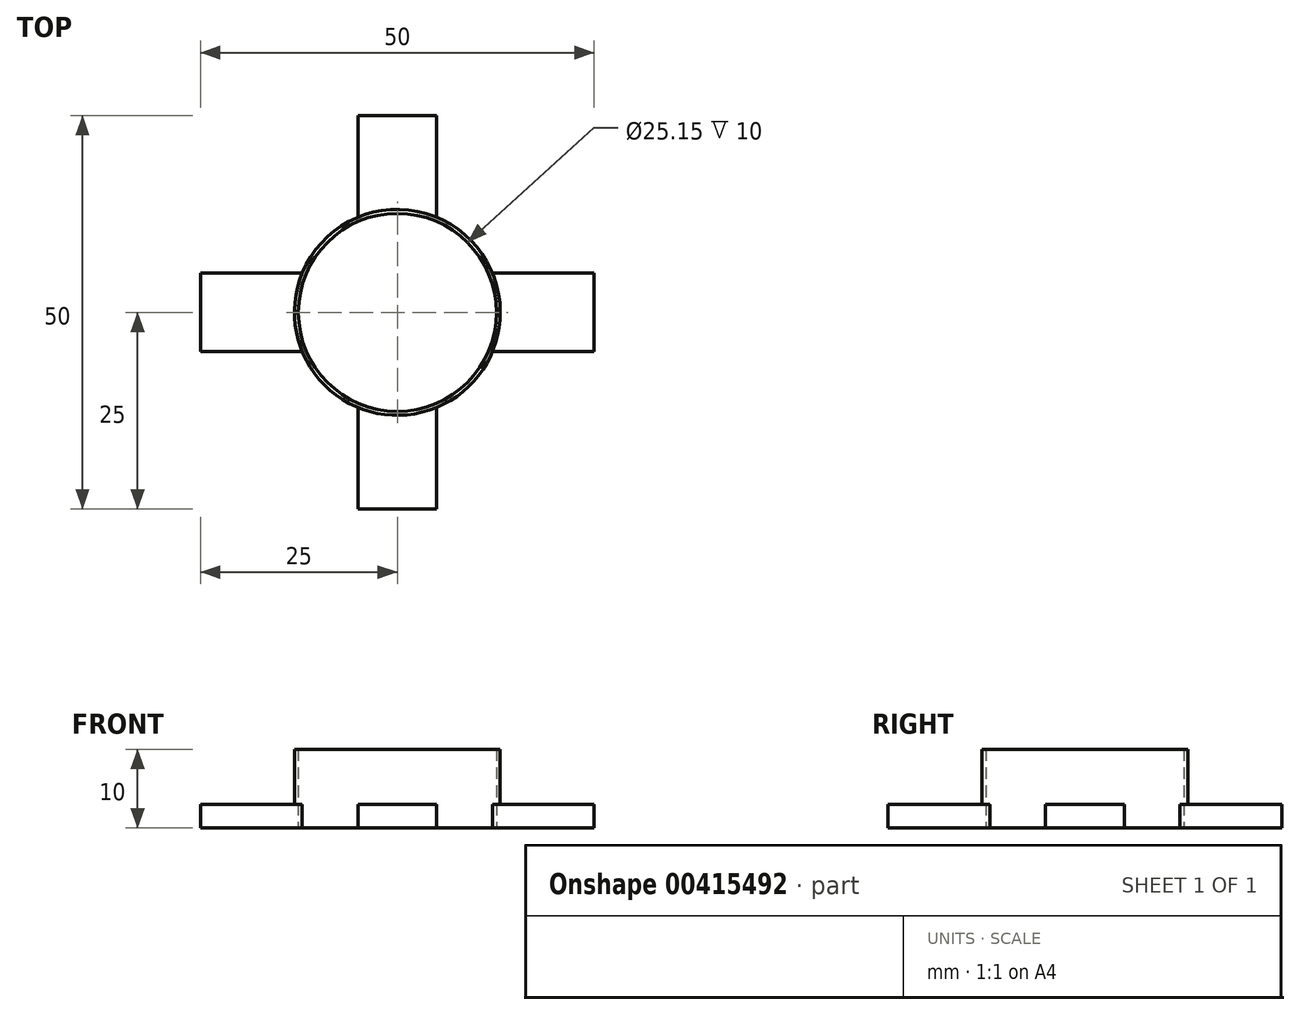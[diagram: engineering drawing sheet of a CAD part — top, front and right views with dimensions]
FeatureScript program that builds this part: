
annotation { "Feature Type Name" : "Feature", "Feature Type Description" : "" }
export const myFeature = defineFeature(function(context is Context, id is Id, definition is map)
    precondition{}
    {
        {
            var Q0;
            Q0=qCreatedBy(makeId("Top.planeOp"),FACE);
            var sketch = newSketch(context, id + "F0", { "sketchPlane" : qUnion([Q0])});
            skCircle(sketch, "E0", {"center": v(0, 0) * mm, "radius": 12.57 * mm});
            skCircle(sketch, "E1", {"center": v(0, 0) * mm, "radius": 13.07 * mm});
            skSolve(sketch);
        }
        {
            var Q0;
            Q0 = qSketchRegion(id + "F0", true);
            extrude(context, id + "F1", {"entities" : qUnion([Q0]), "depth" : 10 * mm});
        }
        {
            var Q0;
            Q0=qCreatedBy(makeId("Top.planeOp"),FACE);
            var sketch = newSketch(context, id + "F2", { "sketchPlane" : qUnion([Q0])});
            skLineSegment(sketch, "E2.bottom", {"start": v(25, -5) * mm, "end": v(-25, -5) * mm});
            skLineSegment(sketch, "E2.top", {"start": v(25, 5) * mm, "end": v(-25, 5) * mm});
            skLineSegment(sketch, "E2.left", {"start": v(25, -5) * mm, "end": v(25, 5) * mm});
            skLineSegment(sketch, "E2.right", {"start": v(-25, -5) * mm, "end": v(-25, 5) * mm});
            skPoint(sketch, "E2.middle", {"position": v(0, 0) * mm});
            skLineSegment(sketch, "E3.bottom", {"start": v(5, -25) * mm, "end": v(-5, -25) * mm});
            skLineSegment(sketch, "E3.top", {"start": v(5, 25) * mm, "end": v(-5, 25) * mm});
            skLineSegment(sketch, "E3.left", {"start": v(5, -25) * mm, "end": v(5, 25) * mm});
            skLineSegment(sketch, "E3.right", {"start": v(-5, -25) * mm, "end": v(-5, 25) * mm});
            skSolve(sketch);
        }
        {
            var Q0;
            Q0 = qSketchRegion(id + "F2", true);
            extrude(context, id + "F3", {"entities" : qUnion([Q0]), "operationType" : NewBodyOperationType.ADD, "depth" : 3 * mm});
        }
        {
            var Q0;
            {var subQ0=sQuery(id+"F2.wireOp",EDGE,"E2.left");var subQ1=sQuery(id+"F2.wireOp",EDGE,"E2.top");var subQ2=sQuery(id+"F2.wireOp",EDGE,"E3.left");var subQ4=sQuery(id+"F2.wireOp",EDGE,"E2.right");var subQ5=sQuery(id+"F2.wireOp",EDGE,"E2.bottom");var subQ6=sQuery(id+"F2.wireOp",EDGE,"E3.right");var subQ9=sQuery(id+"F2.wireOp",EDGE,"E3.top");var subQ10=sQuery(id+"F2.wireOp",EDGE,"E3.bottom");Q0=makeQuery(id+"F3.boolean.opBoolean","SPLIT",FACE,{"disambiguationData":[TD([makeQuery(id+"F1.opExtrude","SWEPT_FACE",FACE,{"disambiguationData":[OSD([sQuery(id+"F0.wireOp",EDGE,"E0")])]})])],"derivedFrom":makeQuery(id+"F3.opExtrude","CAP_FACE",FACE,{"disambiguationData":[OSD([subQ5,subQ1,subQ0,subQ4,subQ10,subQ9,subQ2,subQ6])],"isStart":false})});}
            var sketch = newSketch(context, id + "F4", { "sketchPlane" : qUnion([Q0])});
            skCircle(sketch, "E4.0", {"center": v(0, 0) * mm, "radius": 12.57 * mm});
            skSolve(sketch);
        }
        {
            var Q0;
            Q0 = qSketchRegion(id + "F4", true);
            extrude(context, id + "F5", {"entities" : qUnion([Q0]), "operationType" : NewBodyOperationType.REMOVE, "oppositeDirection" : true, "depth" : 25 * mm});
        }
    });
